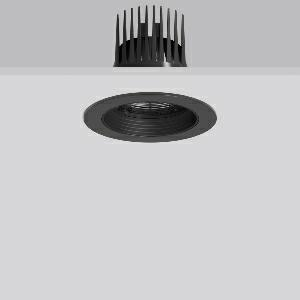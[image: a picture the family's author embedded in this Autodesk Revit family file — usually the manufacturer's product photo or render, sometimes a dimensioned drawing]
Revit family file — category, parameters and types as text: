
# Revit family: heledon_maxi_e_901769_003_2_9b21
name_source: partatom
category: Lighting Fixtures
units: mm (PartAtom-declared; Revit-internal decimal feet)

## family parameters
Cut with Voids When Loaded = No
Host = Face
Light Source = No
Part Type = Normal
Room Calculation Point = No
Round Connector Dimension = Use Diameter
Shared = No

## types (1)
- HELEDON maxi E (1 x LED Modul 927, 3450 lm, 2700)
    Apparent Load = 35 VA
    Approval mark = CE
    CIE Flux Codes = 96 100 100 100 100
    Color Rendering = 92
    Color Temperature = 2700
    Default Elevation = 1800 mm
    Description = Series: HELEDON maxi
Round recessed downlight. Housing: die-cast aluminium, powder-coated. Black plastic ring and recessed LED to prevent glare from the side. Optical assembly with lens made of plastic (polycarbonate) for the best homogeneous light distribution - can be changed without tools. Best colour rendering index Ra>90. Suitable for Recessed ceiling mounting. Installation without tools thanks to spring fastening system. Including separate LED converter with connecting cable 600 mm.High quality converter without flickering and stroboscopic effect. Through-wiring box (5 pole) available as accessory. The following accessories can be mounted without use of tools: interchangeable lenses, decorative glasses, honeycomb louvre, clear and frosted diffusers, white interchangeable plastic ring. 
Colour: deep black, matt (RAL 9005)
Diameter: 162 mm
Height: 3 mm
Cut-out diameter: 152 mm
Recess height: 200 mm
Luminaire: recess height: 135 mm
Lamp: LED
Socket: without socket
Colour temperature: 2700K
Colour rendering index (CRI): 92
System power: 35 W
Rated luminous flux: 3450 lm
Luminous efficiency: 99 lm/W
Control gear: Regulated power supply
Protection class: II
Type of protection: IP 20
    Height = 0 mm  [stored 0 ft]
    Lamp = 1 x LED Modul 927
    Lamp Light Flux = 3450 lm
    Lamp count = 1
    Length = 162 mm
    Lifetime = 50000 h
    Luminous efficacy = 99 lm/W
    Manufacturer = RZB
    ModVariant = No
    Model = 901769.003.2
    Mounting Place = Ceiling
    Mounting Type = Recessed
    Number of Poles = 1
    OnlyDefault = Yes
    Power Factor = 1
    Product Name = HELEDON maxi E
    Product group = Recessed downlights
    ProductGroupID = 402
    Protection Class = Protection class II
    Protection Degree = IP 20
    RLX_Detail_Level = 1
    RLX_Emergency_Light_Flux = 0 lm
    RLX_Emergency_Type = 0
    RLX_Emergency_Type_DB = No
    RlxData = <blob elided: 121165 chars, md5=ae5d8122>
    Socket = socket
    Standby Power = 0 W
    System Light Flux = 3450 lm
    System Power = 35 W
    Type Comments = Product without accessories
    Type Image = 901663.003.jpg
    URL = http://relux.com
    VarID = ---
    Voltage = 230 V
    Voltage Range = 220-240 V
    Weight = 0.00 kg
    Width = 0 mm  [stored 0 ft]

note: [stored X ft] marks values corroborated as IEEE doubles in the binary element streams (Revit-internal decimal feet)

## geometry (parser evidence)
native form markers: Blend x4, Sweep x13
no freeform markers — native parametric forms only
